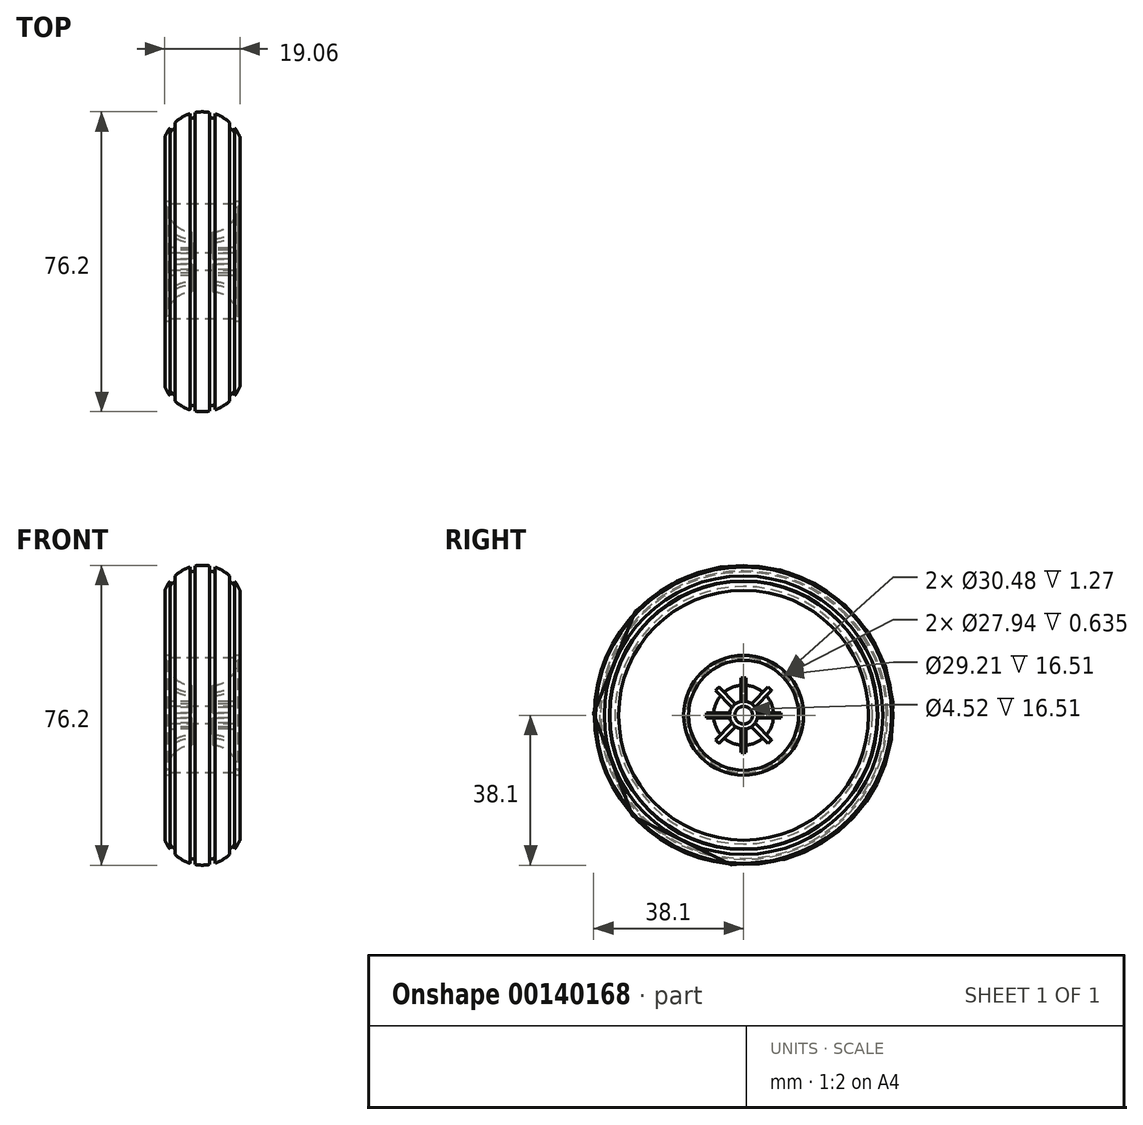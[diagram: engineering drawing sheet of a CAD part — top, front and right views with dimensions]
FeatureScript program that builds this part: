
annotation { "Feature Type Name" : "Feature", "Feature Type Description" : "" }
export const myFeature = defineFeature(function(context is Context, id is Id, definition is map)
    precondition{}
    {
        {
            var Q0;
            Q0=qCreatedBy(makeId("Top.planeOp"),FACE);
            var sketch = newSketch(context, id + "F0", { "sketchPlane" : qUnion([Q0])});
            skLineSegment(sketch, "E0", {"start": v(0, 2.26) * mm, "end": v(8.26, 2.26) * mm});
            skLineSegment(sketch, "E1", {"start": v(8.26, 2.26) * mm, "end": v(8.26, 3.56) * mm});
            skLineSegment(sketch, "E2", {"start": v(8.26, 3.56) * mm, "end": v(2.54, 3.56) * mm});
            skLineSegment(sketch, "E3", {"start": v(2.54, 3.56) * mm, "end": v(2.54, 7.62) * mm});
            skLineSegment(sketch, "E4", {"start": v(8.9, 13.97) * mm, "end": v(9.53, 13.97) * mm});
            skLineSegment(sketch, "E5", {"start": v(9.53, 13.97) * mm, "end": v(9.53, 15.24) * mm});
            skLineSegment(sketch, "E6", {"start": v(9.53, 15.24) * mm, "end": v(8.26, 15.24) * mm});
            skLineSegment(sketch, "E7", {"start": v(8.26, 15.24) * mm, "end": v(8.26, 14.6) * mm});
            skLineSegment(sketch, "E8", {"start": v(8.26, 14.6) * mm, "end": v(0, 14.6) * mm});
            skArc(sketch, "E9", {"start": v(2.54, 7.62) * mm, "mid": v(7.03, 9.48) * mm, "end": v(8.89, 13.97) * mm});
            skLineSegment(sketch, "E10", {"start": v(9.53, 15.24) * mm, "end": v(9.53, 31.75) * mm});
            skLineSegment(sketch, "E11", {"start": v(0, 0) * mm, "end": v(0, 38.1) * mm, "construction": true});
            skLineSegment(sketch, "E12.MirrorCS", {"start": v(-8.26, 2.26) * mm, "end": v(-8.26, 3.56) * mm});
            skLineSegment(sketch, "E13.MirrorCS", {"start": v(-8.26, 15.24) * mm, "end": v(-8.26, 14.6) * mm});
            skLineSegment(sketch, "E14.MirrorCS", {"start": v(-9.53, 13.97) * mm, "end": v(-9.53, 15.24) * mm});
            skLineSegment(sketch, "E15.MirrorCS", {"start": v(-9.53, 15.24) * mm, "end": v(-8.26, 15.24) * mm});
            skLineSegment(sketch, "E16.MirrorCS", {"start": v(-8.9, 13.97) * mm, "end": v(-9.53, 13.97) * mm});
            skLineSegment(sketch, "E17.MirrorCS", {"start": v(0, 2.26) * mm, "end": v(-8.26, 2.26) * mm});
            skArc(sketch, "E18.MirrorCS", {"start": v(-2.54, 7.62) * mm, "mid": v(-7.03, 9.48) * mm, "end": v(-8.89, 13.97) * mm});
            skLineSegment(sketch, "E19.MirrorCS", {"start": v(-8.26, 14.6) * mm, "end": v(0, 14.6) * mm});
            skLineSegment(sketch, "E20.MirrorCS", {"start": v(-2.54, 3.56) * mm, "end": v(-2.54, 7.62) * mm});
            skLineSegment(sketch, "E21.MirrorCS", {"start": v(-8.26, 3.56) * mm, "end": v(-2.54, 3.56) * mm});
            skLineSegment(sketch, "E22.MirrorCS", {"start": v(-9.53, 15.24) * mm, "end": v(-9.53, 31.75) * mm});
            skArc(sketch, "E23", {"start": v(9.52, 31.75) * mm, "mid": v(8.96, 32.9) * mm, "end": v(8.26, 33.97) * mm});
            skLineSegment(sketch, "E24", {"start": v(-10.97, 0) * mm, "end": v(12.8, 0) * mm, "construction": true});
            skLineSegment(sketch, "E25", {"start": v(7.03, 9.48) * mm, "end": v(7.03, 2.9) * mm});
            skLineSegment(sketch, "E26", {"start": v(7.03, 2.9) * mm, "end": v(1.92, 2.9) * mm});
            skLineSegment(sketch, "E27", {"start": v(1.92, 2.9) * mm, "end": v(1.92, 9.5) * mm});
            skLineSegment(sketch, "E28", {"start": v(1.92, 9.5) * mm, "end": v(7.03, 9.48) * mm});
            skPoint(sketch, "E29", {"position": v(8.26, 2.9) * mm});
            skLineSegment(sketch, "E30.MirrorCS", {"start": v(-1.92, 9.5) * mm, "end": v(-7.03, 9.48) * mm});
            skLineSegment(sketch, "E31.MirrorCS", {"start": v(-1.92, 2.9) * mm, "end": v(-1.92, 9.5) * mm});
            skLineSegment(sketch, "E32.MirrorCS", {"start": v(-7.03, 2.9) * mm, "end": v(-1.92, 2.9) * mm});
            skLineSegment(sketch, "E33.MirrorCS", {"start": v(-7.03, 9.48) * mm, "end": v(-7.03, 2.9) * mm});
            skLineSegment(sketch, "E34", {"start": v(1.9, 37.92) * mm, "end": v(1.9, 36.65) * mm});
            skLineSegment(sketch, "E35", {"start": v(8.26, 33.97) * mm, "end": v(8.26, 32.7) * mm});
            skLineSegment(sketch, "E36", {"start": v(6.99, 35.38) * mm, "end": v(6.99, 34.1) * mm});
            skLineSegment(sketch, "E37", {"start": v(3.18, 37.6) * mm, "end": v(3.18, 36.33) * mm});
            skArc(sketch, "E38", {"start": v(1.9, 37.92) * mm, "mid": v(0.96, 38.06) * mm, "end": v(0, 38.1) * mm});
            skArc(sketch, "E39", {"start": v(6.98, 35.38) * mm, "mid": v(5.2, 36.7) * mm, "end": v(3.18, 37.6) * mm});
            skArc(sketch, "E40", {"start": v(8.26, 32.7) * mm, "mid": v(7.65, 33.43) * mm, "end": v(6.99, 34.1) * mm});
            skArc(sketch, "E41", {"start": v(3.17, 36.33) * mm, "mid": v(2.55, 36.51) * mm, "end": v(1.9, 36.65) * mm});
            skLineSegment(sketch, "E42.MirrorCS", {"start": v(-6.99, 35.38) * mm, "end": v(-6.99, 34.1) * mm});
            skLineSegment(sketch, "E43.MirrorCS", {"start": v(-8.26, 33.97) * mm, "end": v(-8.26, 32.7) * mm});
            skArc(sketch, "E44.MirrorCS", {"start": v(-8.26, 32.7) * mm, "mid": v(-7.65, 33.43) * mm, "end": v(-6.99, 34.1) * mm});
            skArc(sketch, "E45.MirrorCS", {"start": v(-3.17, 36.33) * mm, "mid": v(-2.55, 36.51) * mm, "end": v(-1.9, 36.65) * mm});
            skLineSegment(sketch, "E46.MirrorCS", {"start": v(-3.18, 37.6) * mm, "end": v(-3.18, 36.33) * mm});
            skArc(sketch, "E47.MirrorCS", {"start": v(-9.52, 31.75) * mm, "mid": v(-8.96, 32.9) * mm, "end": v(-8.26, 33.97) * mm});
            skArc(sketch, "E48.MirrorCS", {"start": v(-1.9, 37.92) * mm, "mid": v(-0.96, 38.06) * mm, "end": v(0, 38.1) * mm});
            skLineSegment(sketch, "E49.MirrorCS", {"start": v(-1.9, 37.92) * mm, "end": v(-1.9, 36.65) * mm});
            skArc(sketch, "E50.MirrorCS", {"start": v(-6.98, 35.38) * mm, "mid": v(-5.2, 36.7) * mm, "end": v(-3.18, 37.6) * mm});
            skSolve(sketch);
        }
        {
            var Q0;
            Q0=makeQuery(id+"F0.imprint","IMPRINT",FACE,{"disambiguationData":[TD([[makeQuery(id+"F0.imprint","IMPRINT",EDGE,{"derivedFrom":sQuery(id+"F0.wireOp",EDGE,"E0")}),1.0]])]});
            var Q1;
            {var subQ5=sQuery(id+"F0.wireOp",EDGE,"E3");Q1=makeQuery(id+"F0.imprint","IMPRINT",FACE,{"disambiguationData":[TD([[makeQuery(id+"F0.imprint","IMPRINT",EDGE,{"derivedFrom":subQ5}),1.0]])]});}
            var Q2;
            {var subQ2=sQuery(id+"F0.wireOp",EDGE,"E20.MirrorCS");Q2=makeQuery(id+"F0.imprint","IMPRINT",FACE,{"disambiguationData":[TD([[makeQuery(id+"F0.imprint","IMPRINT",EDGE,{"derivedFrom":subQ2}),-1.0]])]});}
            var Q3;
            Q3=sQuery(id+"F0.wireOp",EDGE,"E24");
            revolve(context, id + "F1", {"entities" : qUnion([Q0, Q1, Q2]), "axis" : qUnion([Q3]), "revolveType" : RevolveType.FULL});
        }
        {
            var Q0;
            {var subQ5=sQuery(id+"F0.wireOp",EDGE,"E3");Q0=makeQuery(id+"F0.imprint","IMPRINT",FACE,{"disambiguationData":[TD([[makeQuery(id+"F0.imprint","IMPRINT",EDGE,{"derivedFrom":subQ5}),1.0]])]});}
            var Q1;
            {var subQ0=sQuery(id+"F0.wireOp",EDGE,"E3");Q1=makeQuery(id+"F0.imprint","IMPRINT",FACE,{"disambiguationData":[TD([[makeQuery(id+"F0.imprint","IMPRINT",EDGE,{"derivedFrom":subQ0}),-1.0]])]});}
            var Q2;
            {var subQ2=sQuery(id+"F0.wireOp",EDGE,"E20.MirrorCS");Q2=makeQuery(id+"F0.imprint","IMPRINT",FACE,{"disambiguationData":[TD([[makeQuery(id+"F0.imprint","IMPRINT",EDGE,{"derivedFrom":subQ2}),-1.0]])]});}
            var Q3;
            {var subQ0=sQuery(id+"F0.wireOp",EDGE,"E20.MirrorCS");Q3=makeQuery(id+"F0.imprint","IMPRINT",FACE,{"disambiguationData":[TD([[makeQuery(id+"F0.imprint","IMPRINT",EDGE,{"derivedFrom":subQ0}),1.0]])]});}
            extrude(context, id + "F2", {"entities" : qUnion([Q0, Q1, Q2, Q3]), "endBound" : BoundingType.SYMMETRIC, "depth" : 1.27 * mm});
        }
        {
            var Q0;
            Q0=makeQuery(id+"F2.opExtrude","SWEPT_BODY",BODY,{"disambiguationData":[OSD([sQuery(id+"F0.wireOp",EDGE,"E25"),sQuery(id+"F0.wireOp",EDGE,"E26"),sQuery(id+"F0.wireOp",EDGE,"E27"),sQuery(id+"F0.wireOp",EDGE,"E28")])]});
            var Q1;
            Q1=makeQuery(id+"F2.opExtrude","SWEPT_BODY",BODY,{"disambiguationData":[OSD([sQuery(id+"F0.wireOp",EDGE,"E30.MirrorCS"),sQuery(id+"F0.wireOp",EDGE,"E31.MirrorCS"),sQuery(id+"F0.wireOp",EDGE,"E32.MirrorCS"),sQuery(id+"F0.wireOp",EDGE,"E33.MirrorCS")])]});
            var Q2;
            Q2=sQuery(id+"F0.wireOp",EDGE,"E24");
            circularPattern(context, id + "F3", {"operationType" : NewBodyOperationType.ADD, "entities" : qUnion([Q0, Q1]), "axis" : qUnion([Q2]), "angle" : 45 * degree, "instanceCount" : 8});
        }
        {
            var Q0;
            Q0=makeQuery(id+"F0.imprint","IMPRINT",FACE,{"disambiguationData":[TD([[makeQuery(id+"F0.imprint","IMPRINT",EDGE,{"derivedFrom":sQuery(id+"F0.wireOp",EDGE,"E6")}),-1.0]])]});
            var Q1;
            Q1=sQuery(id+"F0.wireOp",EDGE,"E24");
            revolve(context, id + "F4", {"entities" : qUnion([Q0]), "axis" : qUnion([Q1]), "revolveType" : RevolveType.FULL});
        }
    });
